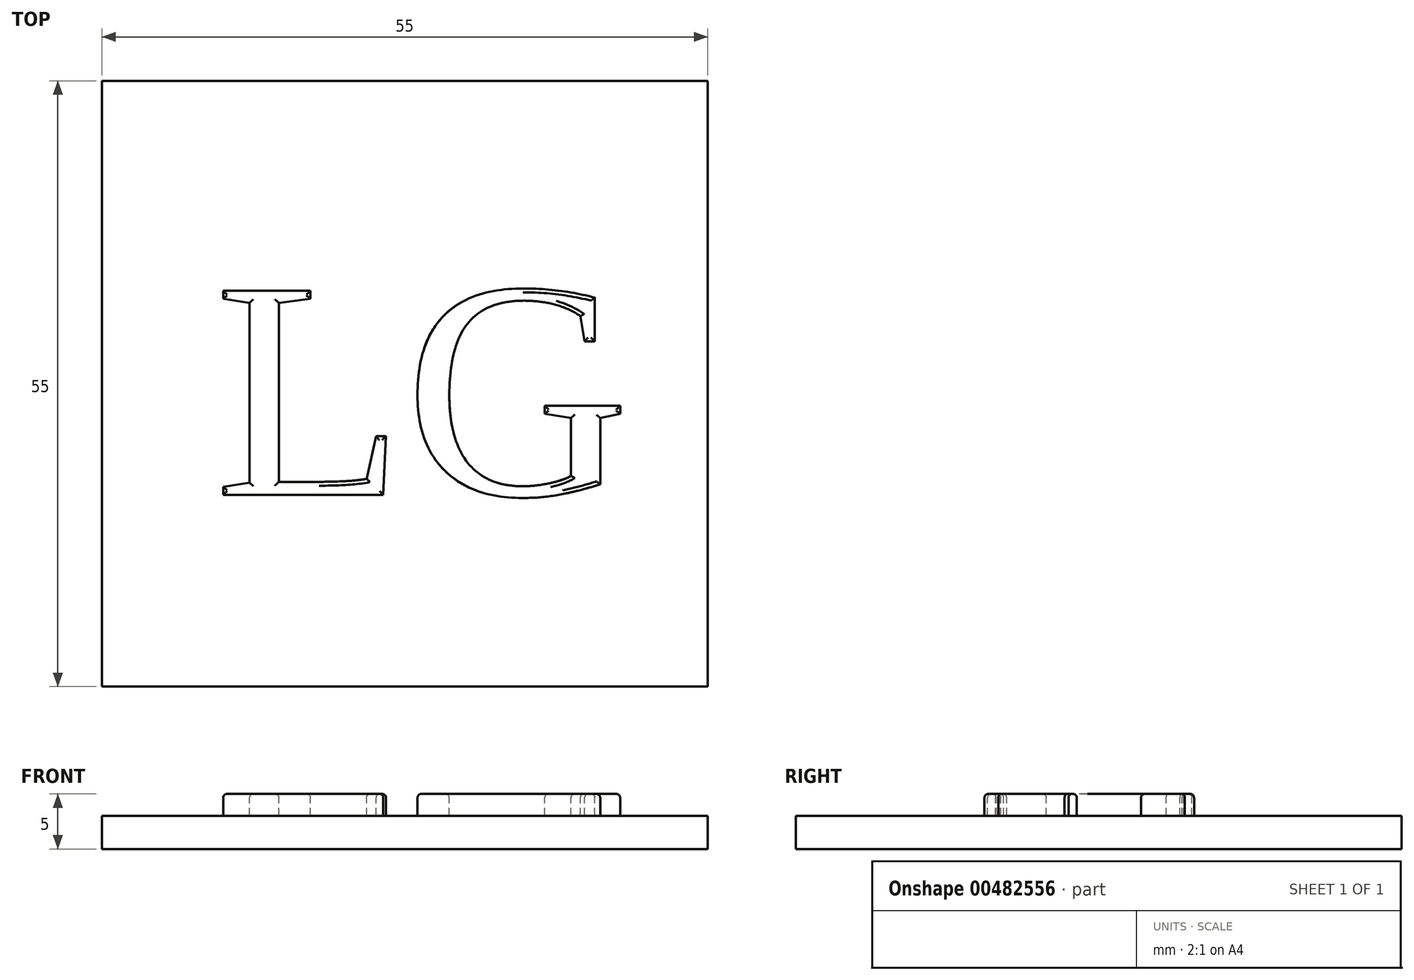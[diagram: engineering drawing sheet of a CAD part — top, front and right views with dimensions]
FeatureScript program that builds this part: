
annotation { "Feature Type Name" : "Feature", "Feature Type Description" : "" }
export const myFeature = defineFeature(function(context is Context, id is Id, definition is map)
    precondition{}
    {
        {
            var Q0;
            Q0=qCreatedBy(makeId("Top.planeOp"),FACE);
            var sketch = newSketch(context, id + "F0", { "sketchPlane" : qUnion([Q0])});
            skLineSegment(sketch, "E0.bottom", {"start": v(0, 0) * mm, "end": v(55, 0) * mm});
            skLineSegment(sketch, "E0.top", {"start": v(0, -55) * mm, "end": v(55, -55) * mm});
            skLineSegment(sketch, "E0.left", {"start": v(0, 0) * mm, "end": v(0, -55) * mm});
            skLineSegment(sketch, "E0.right", {"start": v(55, 0) * mm, "end": v(55, -55) * mm});
            skSolve(sketch);
        }
        {
            var Q0;
            Q0=makeQuery(id+"F0.imprint","IMPRINT",FACE,{"disambiguationData":[TD([[makeQuery(id+"F0.imprint","IMPRINT",EDGE,{"derivedFrom":sQuery(id+"F0.wireOp",EDGE,"E0.bottom")}),-1.0]])]});
            extrude(context, id + "F1", {"entities" : qUnion([Q0]), "depth" : 5 * mm});
        }
        {
            var Q0;
            Q0=makeQuery(id+"F1.opExtrude","CAP_FACE",FACE,{"disambiguationData":[OSD([sQuery(id+"F0.wireOp",EDGE,"E0.bottom"),sQuery(id+"F0.wireOp",EDGE,"E0.top"),sQuery(id+"F0.wireOp",EDGE,"E0.left"),sQuery(id+"F0.wireOp",EDGE,"E0.right")])],"isStart":false});
            var sketch = newSketch(context, id + "F2", { "sketchPlane" : qUnion([Q0])});
            skText(sketch, "E1", { "text": "LG", "fontName": "Tinos-Regular.ttf"});
            const initialGuessF2  = {"E1": [0.0102, -0.0376, 1, 0, 0.02038]};
            skSetInitialGuess(sketch, initialGuessF2);
            skSolve(sketch);
        }
        {
            var Q0;
            Q0=makeQuery(id+"F2.imprint","IMPRINT",FACE,{"disambiguationData":[TD([[makeQuery(id+"F2.imprint","IMPRINT",EDGE,{"derivedFrom":sQuery(id+"F2.wireOp",EDGE,"E1.sketch_text.stroke-0")}),1.0]])]});
            extrude(context, id + "F3", {"entities" : qUnion([Q0]), "operationType" : NewBodyOperationType.REMOVE, "oppositeDirection" : true, "depth" : 2 * mm});
        }
        {
            var Q0;
            Q0=makeQuery(id+"F3.boolean.opBoolean","SPLIT",FACE,{"disambiguationData":[TD([makeQuery(id+"F3.opExtrude","SWEPT_FACE",FACE,{"disambiguationData":[OSD([sQuery(id+"F2.wireOp",EDGE,"E1.sketch_text.stroke-0")])]})])],"derivedFrom":makeQuery(id+"F1.opExtrude","CAP_FACE",FACE,{"disambiguationData":[OSD([sQuery(id+"F0.wireOp",EDGE,"E0.bottom"),sQuery(id+"F0.wireOp",EDGE,"E0.top"),sQuery(id+"F0.wireOp",EDGE,"E0.left"),sQuery(id+"F0.wireOp",EDGE,"E0.right")])],"isStart":false})});
            var Q1;
            Q1=makeQuery(id+"F3.boolean.opBoolean","SPLIT",FACE,{"disambiguationData":[TD([makeQuery(id+"F3.opExtrude","SWEPT_FACE",FACE,{"disambiguationData":[OSD([sQuery(id+"F2.wireOp",EDGE,"E1.sketch_text.stroke-15")])]})])],"derivedFrom":makeQuery(id+"F1.opExtrude","CAP_FACE",FACE,{"disambiguationData":[OSD([sQuery(id+"F0.wireOp",EDGE,"E0.bottom"),sQuery(id+"F0.wireOp",EDGE,"E0.top"),sQuery(id+"F0.wireOp",EDGE,"E0.left"),sQuery(id+"F0.wireOp",EDGE,"E0.right")])],"isStart":false})});
            fillet(context, id + "F4", {"entities" : qUnion([Q0, Q1]), "radius" : 0.35 * mm, "tangentPropagation" : true, "allowEdgeOverflow" : false});
        }
    });
